FCSTD DOCUMENT  (FreeCAD 0.19R19373 (Git))
Label: asm_base_serv0_v019_2
License: All rights reserved
LicenseURL: http://en.wikipedia.org/wiki/All_rights_reserved
objects: App::DocumentObjectGroup×2, App::Link×2, PartDesign::CoordinateSystem×1, App::FeaturePython×1, App::Part×1
note: 1 computed .brp shape members not serialized (recipe doc carries the construction recipe); baked Part::Feature solids carry a one-line shape summary decoded from their .brp
EXTERNAL_REF file=futuba_s3003_2.FCStd obj=LCS_Origin
EXTERNAL_REF file=futuba_s3003_2.FCStd obj=Model

FEATURE [App::DocumentObjectGroup] Parts
FEATURE [PartDesign::CoordinateSystem] LCS_Origin
  AttacherType = Attacher::AttachEngine3D
  MapMode = 2
  Support = -> [X_Axis]
FEATURE [App::DocumentObjectGroup] Constraints
FEATURE [App::FeaturePython] Variables  # WARN: FeaturePython — macro-defined, semantics opaque (R4)
FEATURE [App::Link] futuba_s3003_2
  AssemblyType = Asm4EE
  AttachedBy = #LCS_Origin
  AttachedTo = Parent Assembly#LCS_Origin
  LinkedObject = -> <external futuba_s3003_2.FCStd>#Model
  expr: Placement = LCS_Origin.Placement * AttachmentOffset * futuba_s3003_2#LCS_Origin.Placement ^ -1
FEATURE [App::Link] futuba_s3003_2001
  AssemblyType = Asm4EE
  AttachedBy = #LCS_Origin
  AttachedTo = futuba_s3003_2#LCS_Origin
  LinkedObject = -> <external futuba_s3003_2.FCStd>#Model
  expr: Placement = futuba_s3003_2.Placement * futuba_s3003_2#LCS_Origin.Placement * AttachmentOffset * futuba_s3003_2#LCS_Origin.Placement ^ -1
FEATURE [App::Part] Model
  Configuration = 0
  Group = -> [LCS_Origin,Constraints,Variables,futuba_s3003_2,futuba_s3003_2001]
  Origin = -> Origin
  Type = Assembly4 Model
